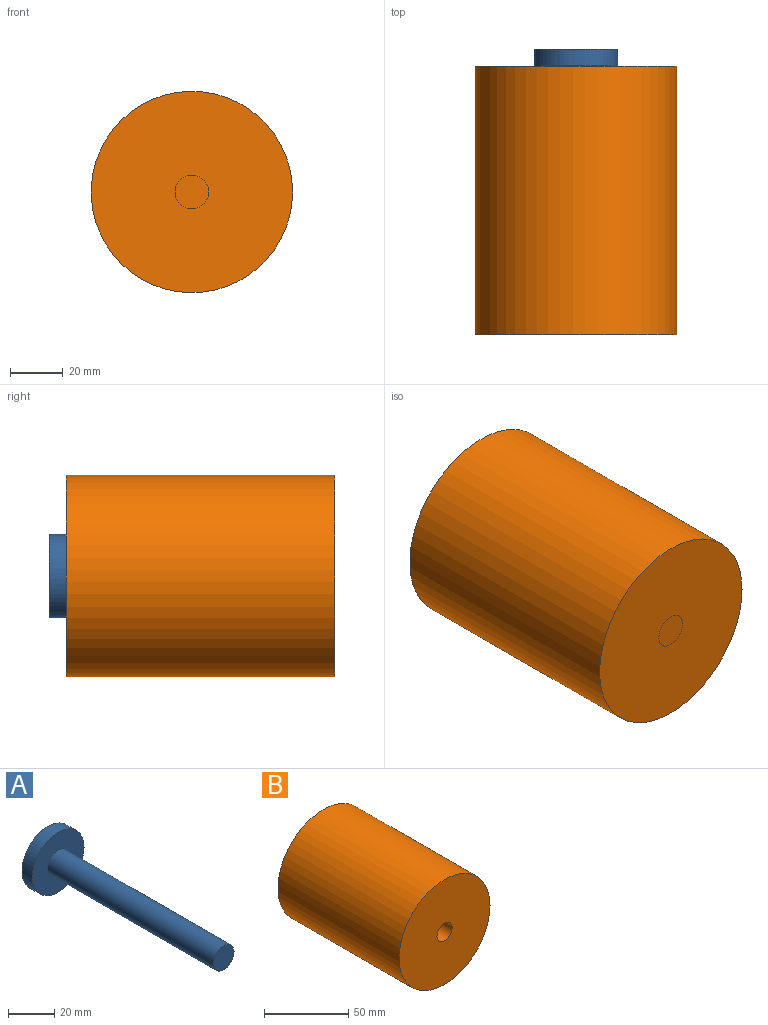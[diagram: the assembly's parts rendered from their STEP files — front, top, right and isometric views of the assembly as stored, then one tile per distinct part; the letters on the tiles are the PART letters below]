
ASSEMBLY  parts=2 mates=1
PART A: 5 faces, bbox 31.8x108x31.8 mm
  f0: cylinder r=6.35mm len=101.6mm, axis (0,1,0), area 4053.7mm2, adj f1,f4
  f1: plane 12.7x12.7mm, normal (0,-1,0), area 126.7mm2, adj f0
  f2: cylinder r=15.88mm len=31.75mm, axis (0,-1,0), area 633.4mm2, adj f3,f4
  f3: plane 31.75x31.75mm, normal (0,1,0), area 791.7mm2, adj f2
  f4: plane 31.75x31.75mm, normal (0,-1,0), area 665.1mm2, adj f0,f2
PART B: 5 faces, bbox 76.2x101.6x76.2 mm
  f0: cylinder r=38.1mm len=101.6mm, axis (0,1,0), area 24322mm2, adj f1,f2
  f1: plane 76.2x76.2mm, normal (0,-1,0), area 4433.7mm2, adj f0,f3
  f2: plane 76.2x76.2mm, normal (0,1,0), area 4560.4mm2, adj f0
  f3: cylinder r=6.35mm len=76.2mm, axis (0,1,0), area 3040.2mm2, adj f1,f4
  f4: plane 12.7x12.7mm, normal (0,-1,0), area 126.7mm2, adj f3
PLACE A t=(11.32,12.61,44.09)mm
PLACE B rot(axis=(1,0,0),180deg) t=(11.32,-63.66,44.09)mm
MATE slider B.f0 <-> A.f0  axis (0,1,0) through (11.32,12.54,44.09)mm
